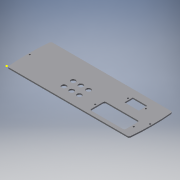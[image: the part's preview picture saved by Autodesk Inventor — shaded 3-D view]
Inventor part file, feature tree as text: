
AUTODESK INVENTOR PART (.ipt)
format: ipt  version: 2018 (Build 220112000, 112)  size: 205,312 bytes
history: native  units: mm
features: sketch x5, extrude x3, hole x1
ambient origin geometry x8: Origin, YZ Plane, XZ Plane, XY Plane, X Axis, Y Axis, Z Axis, Center Point
bodies: Volumenkörper1 (feature_tree)
feature tree (9):
  extrude  "Extrusion1"  Depth=85.0mm
  hole  "Bohrung1"  [1 undecoded]
  extrude  "Extrusion2"  Depth=2.0mm
  sketch  "Sketch7"  dims[d7=452.5625mm d8=452.5625mm]
  extrude  "Extrusion5"  Depth=452.5625mm
  sketch  "Skizze1"  dims[d0=85.0mm d1=242.0mm]
  sketch  "Skizze2"  dims[d2=2.0mm d3=2.0mm]
  sketch  "Skizze3"  dims[d4=2.0mm d5=905.125mm d6=905.125mm]
  sketch  "Sketch8"  dims[d9=2.5mm d10=0.0mm d11=42.5mm d12=42.5mm d13=235.8mm d14=117.9mm d15=117.9mm d16=3.3mm d17=6.0mm d18=4.0mm d19=2.0mm d20=90.0deg d21=8.0mm d22=20.594885mm d23=9.599311mm d24=9.599311mm d25=2.5mm d26=2.5mm d27=5.0mm d28=0.0mm d75=3.2mm d76=75.5mm d77=3.2mm d78=68.0mm d79=29.2mm d80=3.1mm d81=22.0mm d82=11.15mm d85=3.0mm d86=0.0mm d87=45.0mm d89=28.0mm d90=16.5mm d91=3.2mm d92=5.0mm d93=3.2mm d94=5.0mm d95=10.5mm d96=10.5mm d97=45.0mm d98=1.0mm d99=9.4mm d101=9.4mm d103=9.4mm d113=35.0mm d114=15.0mm d115=15.0mm d116=9.4mm d118=9.4mm d120=9.4mm d122=15.0mm d123=15.0mm d125=22.0mm d126=40.0mm d128=8.85mm d129=4.15mm]
note: 1 required parameter value undecoded (feature->parameter linkage not recoverable at this tier; creation-order binding heuristic only, values carry confidence <= 0.55)
